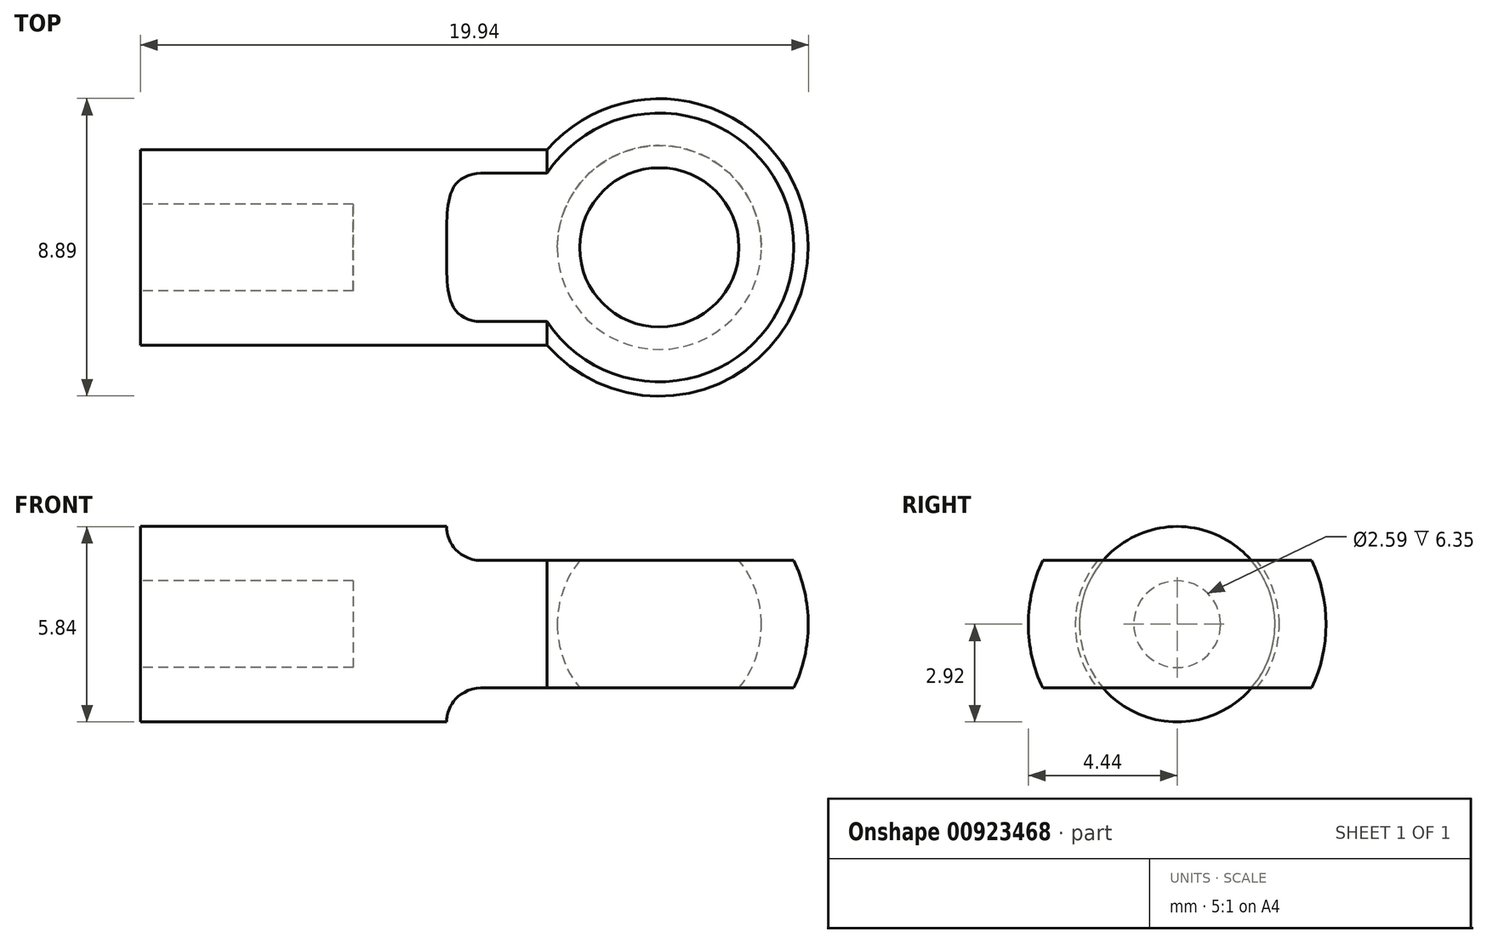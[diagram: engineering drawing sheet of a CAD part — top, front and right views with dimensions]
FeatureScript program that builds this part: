
annotation { "Feature Type Name" : "Feature", "Feature Type Description" : "" }
export const myFeature = defineFeature(function(context is Context, id is Id, definition is map)
    precondition{}
    {
        {
            var Q0;
            Q0=qCreatedBy(makeId("Top.planeOp"),FACE);
            var sketch = newSketch(context, id + "F0", { "sketchPlane" : qUnion([Q0])});
            skArc(sketch, "E0", {"start": v(4.45, 0) * mm, "mid": v(0, 4.45) * mm, "end": v(-4.45, 0) * mm});
            skLineSegment(sketch, "E1", {"start": v(-19.65, 0) * mm, "end": v(19.58, 0) * mm, "construction": true});
            skLineSegment(sketch, "E2", {"start": v(-4.45, 0) * mm, "end": v(4.45, 0) * mm});
            skSolve(sketch);
        }
        {
            var Q0;
            Q0 = qSketchRegion(id + "F0", true);
            var Q1;
            Q1=sQuery(id+"F0.wireOp",EDGE,"E1");
            revolve(context, id + "F1", {"surfaceOperationType" : NewSurfaceOperationType.NEW, "entities" : qUnion([Q0]), "axis" : qUnion([Q1]), "revolveType" : RevolveType.FULL});
        }
        {
            var Q0;
            Q0=qCreatedBy(makeId("Top.planeOp"),FACE);
            var sketch = newSketch(context, id + "F2", { "sketchPlane" : qUnion([Q0])});
            skLineSegment(sketch, "E3", {"start": v(-20.03, 0) * mm, "end": v(11.86, 0) * mm, "construction": true});
            skLineSegment(sketch, "E4", {"start": v(-15.5, 0) * mm, "end": v(-15.5, 2.92) * mm});
            skLineSegment(sketch, "E5", {"start": v(-15.5, 2.92) * mm, "end": v(0, 2.92) * mm});
            skLineSegment(sketch, "E6", {"start": v(0, 2.92) * mm, "end": v(0, 0) * mm});
            skLineSegment(sketch, "E7", {"start": v(0, 0) * mm, "end": v(-15.5, 0) * mm});
            skSolve(sketch);
        }
        {
            var Q0;
            Q0 = qSketchRegion(id + "F2", true);
            var Q1;
            Q1=sQuery(id+"F2.wireOp",EDGE,"E3");
            revolve(context, id + "F3", {"operationType" : NewBodyOperationType.ADD, "surfaceOperationType" : NewSurfaceOperationType.NEW, "entities" : qUnion([Q0]), "axis" : qUnion([Q1]), "revolveType" : RevolveType.FULL});
        }
        {
            var Q0;
            Q0=makeQuery(id+"F3.opRevolve","SWEPT_FACE",FACE,{"disambiguationData":[OSD([sQuery(id+"F2.wireOp",EDGE,"E4")])]});
            var sketch = newSketch(context, id + "F4", { "sketchPlane" : qUnion([Q0])});
            skCircle(sketch, "E8", {"center": v(0, 0) * mm, "radius": 1.3 * mm});
            skSolve(sketch);
        }
        {
            var Q0;
            Q0 = qSketchRegion(id + "F4", true);
            extrude(context, id + "F5", {"entities" : qUnion([Q0]), "operationType" : NewBodyOperationType.REMOVE, "oppositeDirection" : true, "depth" : 6.35 * mm, "offsetDistance" : 25.4 * mm});
        }
        {
            var Q0;
            Q0=qCreatedBy(makeId("Top.planeOp"),FACE);
            var sketch = newSketch(context, id + "F6", { "sketchPlane" : qUnion([Q0])});
            skArc(sketch, "E9", {"start": v(3.05, 0) * mm, "mid": v(0, 3.05) * mm, "end": v(-3.05, 0) * mm});
            skLineSegment(sketch, "E10", {"start": v(-23.57, 0) * mm, "end": v(22.78, 0) * mm, "construction": true});
            skLineSegment(sketch, "E11", {"start": v(-3.05, 0) * mm, "end": v(3.05, 0) * mm});
            skSolve(sketch);
        }
        {
            var Q0;
            Q0 = qSketchRegion(id + "F6", true);
            var Q1;
            Q1=sQuery(id+"F6.wireOp",EDGE,"E10");
            revolve(context, id + "F7", {"operationType" : NewBodyOperationType.REMOVE, "surfaceOperationType" : NewSurfaceOperationType.NEW, "entities" : qUnion([Q0]), "axis" : qUnion([Q1]), "revolveType" : RevolveType.FULL, "oppositeDirection" : true});
        }
        {
            var Q0;
            Q0=qCreatedBy(makeId("Front.planeOp"),FACE);
            var sketch = newSketch(context, id + "F8", { "sketchPlane" : qUnion([Q0])});
            skLineSegment(sketch, "E12", {"start": v(-34.33, 0) * mm, "end": v(22.18, 0) * mm, "construction": true});
            skLineSegment(sketch, "E13", {"start": v(4.02, 1.9) * mm, "end": v(-5.33, 1.9) * mm});
            skArc(sketch, "E14", {"start": v(4.02, 1.9) * mm, "mid": v(0.6, 4.4) * mm, "end": v(-3.35, 2.92) * mm});
            skLineSegment(sketch, "E15", {"start": v(-6.35, 2.92) * mm, "end": v(-3.35, 2.92) * mm});
            skArc(sketch, "E16", {"start": v(-6.35, 2.92) * mm, "mid": v(-6.05, 2.2) * mm, "end": v(-5.33, 1.9) * mm});
            skArc(sketch, "E17.MirrorCS", {"start": v(-6.35, -2.92) * mm, "mid": v(-6.05, -2.2) * mm, "end": v(-5.33, -1.9) * mm});
            skLineSegment(sketch, "E18.MirrorCS", {"start": v(-6.35, -2.92) * mm, "end": v(-3.35, -2.92) * mm});
            skLineSegment(sketch, "E19.MirrorCS", {"start": v(4.02, -1.9) * mm, "end": v(-5.33, -1.9) * mm});
            skArc(sketch, "E20.MirrorCS", {"start": v(4.02, -1.9) * mm, "mid": v(0.6, -4.4) * mm, "end": v(-3.35, -2.92) * mm});
            skSolve(sketch);
        }
        {
            var Q0;
            Q0 = qSketchRegion(id + "F8", true);
            extrude(context, id + "F9", {"entities" : qUnion([Q0]), "operationType" : NewBodyOperationType.REMOVE, "endBound" : BoundingType.THROUGH_ALL, "oppositeDirection" : true, "depth" : 25.4 * mm, "offsetDistance" : 25.4 * mm, "hasSecondDirection" : true, "secondDirectionBound" : SecondDirectionBoundingType.THROUGH_ALL, "secondDirectionOppositeDirection" : false, "secondDirectionDepth" : 25.4 * mm});
        }
    });
